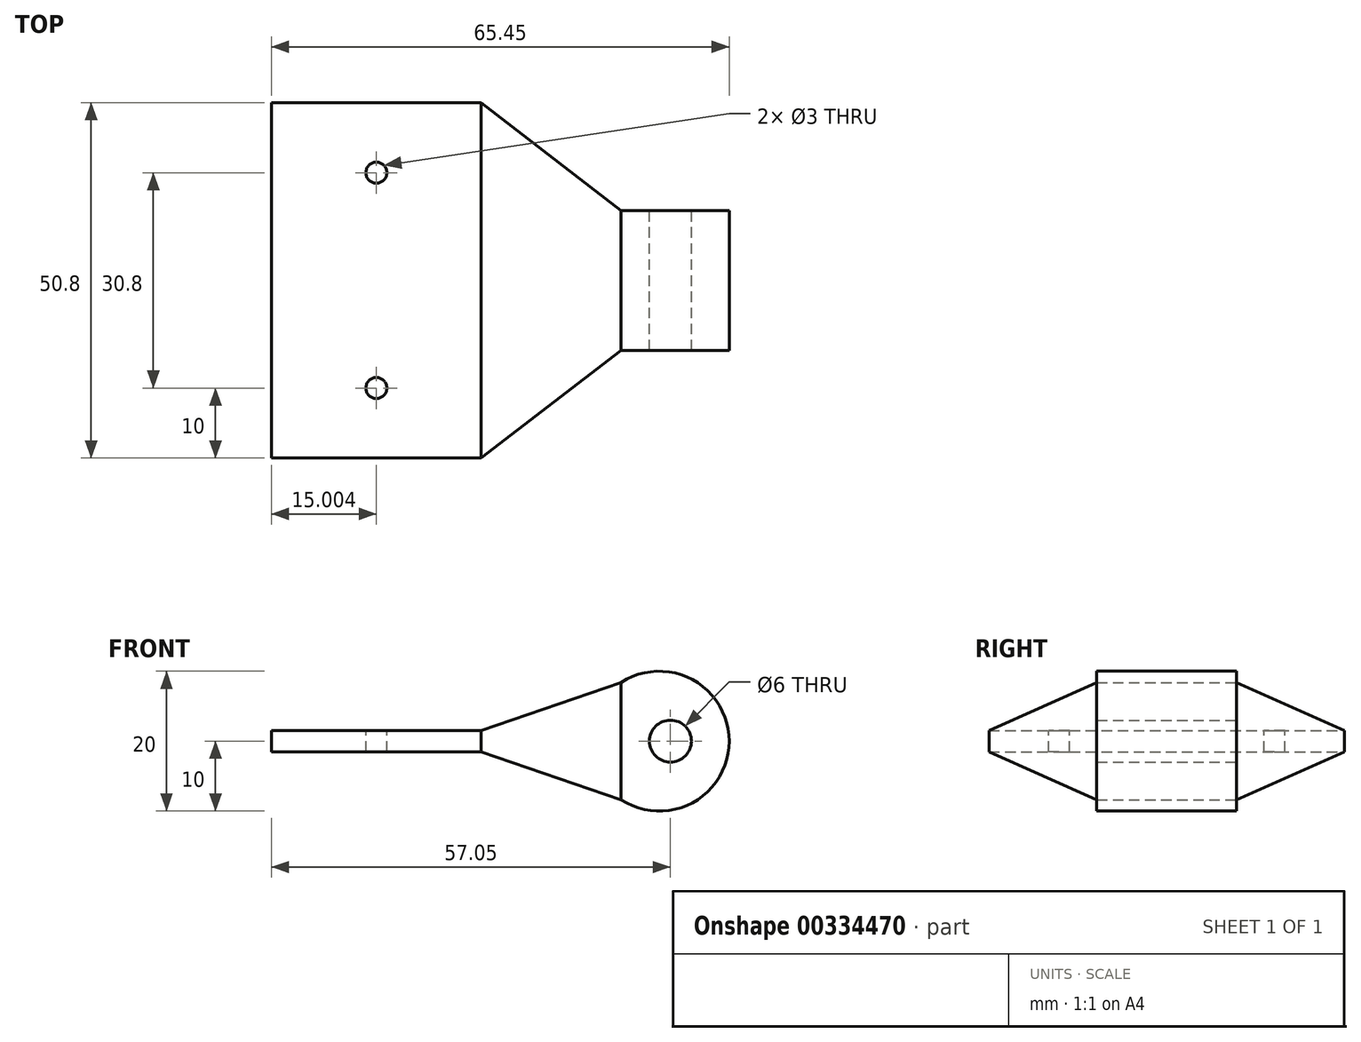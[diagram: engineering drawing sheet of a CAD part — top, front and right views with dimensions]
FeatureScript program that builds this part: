
annotation { "Feature Type Name" : "Feature", "Feature Type Description" : "" }
export const myFeature = defineFeature(function(context is Context, id is Id, definition is map)
    precondition{}
    {
        {
            var Q0;
            Q0=qCreatedBy(makeId("Front.planeOp"),FACE);
            var sketch = newSketch(context, id + "F0", { "sketchPlane" : qUnion([Q0])});
            skArc(sketch, "E0", {"start": v(-5.45, -8.39) * mm, "mid": v(10, 0) * mm, "end": v(-5.45, 8.39) * mm});
            skLineSegment(sketch, "E1", {"start": v(-5.45, 8.39) * mm, "end": v(-5.45, -8.39) * mm});
            skSolve(sketch);
        }
        {
            var Q0;
            Q0=makeQuery(id+"F0.imprint","IMPRINT",FACE,{"disambiguationData":[TD([[makeQuery(id+"F0.imprint","IMPRINT",EDGE,{"derivedFrom":sQuery(id+"F0.wireOp",EDGE,"E0")}),1.0]])]});
            extrude(context, id + "F1", {"entities" : qUnion([Q0]), "endBound" : BoundingType.SYMMETRIC, "depth" : 20 * mm, "offsetDistance" : 25 * mm});
        }
        {
            var Q0;
            Q0=makeQuery(id+"F1.opExtrude","CAP_FACE",FACE,{"disambiguationData":[OSD([sQuery(id+"F0.wireOp",EDGE,"E0"),sQuery(id+"F0.wireOp",EDGE,"E1")])],"isStart":true});
            var sketch = newSketch(context, id + "F2", { "sketchPlane" : qUnion([Q0])});
            skCircle(sketch, "E2", {"center": v(-1.6, 0) * mm, "radius": 3 * mm});
            skSolve(sketch);
        }
        {
            var Q0;
            Q0=sQuery(id+"F2.wireOp",VERTEX,"E2.center");
            var Q1;
            Q1=makeQuery(id+"F1.opExtrude","SWEPT_BODY",BODY,{"disambiguationData":[OSD([sQuery(id+"F0.wireOp",EDGE,"E0"),sQuery(id+"F0.wireOp",EDGE,"E1")])]});
            hole(context, id + "F3", {"style" : HoleStyle.SIMPLE, "endStyle" : HoleEndStyle.THROUGH, "holeDiameter" : 6 * mm, "isTappedThrough" : true, "tappedDepth" : 12 * mm, "tapClearance" : 3, "locations" : qUnion([Q0]), "scope" : qUnion([Q1])});
        }
        {
            var Q0;
            Q0=qCreatedBy(makeId("Front.planeOp"),FACE);
            var sketch = newSketch(context, id + "F4", { "sketchPlane" : qUnion([Q0])});
            skLineSegment(sketch, "E3.bottom", {"start": v(-25.45, 0) * mm, "end": v(-55.45, 0) * mm});
            skLineSegment(sketch, "E3.top", {"start": v(-25.45, 1.5) * mm, "end": v(-55.45, 1.5) * mm});
            skLineSegment(sketch, "E3.left", {"start": v(-25.45, 0) * mm, "end": v(-25.45, 1.5) * mm});
            skLineSegment(sketch, "E3.right", {"start": v(-55.45, 0) * mm, "end": v(-55.45, 1.5) * mm});
            skLineSegment(sketch, "E4.top", {"start": v(-25.45, -1.5) * mm, "end": v(-55.45, -1.5) * mm});
            skLineSegment(sketch, "E4.left", {"start": v(-25.45, 0) * mm, "end": v(-25.45, -1.5) * mm});
            skLineSegment(sketch, "E4.right", {"start": v(-55.45, 0) * mm, "end": v(-55.45, -1.5) * mm});
            skSolve(sketch);
        }
        {
            var Q0;
            Q0=makeQuery(id+"F4.imprint","IMPRINT",FACE,{"disambiguationData":[TD([[makeQuery(id+"F4.imprint","IMPRINT",EDGE,{"derivedFrom":sQuery(id+"F4.wireOp",EDGE,"E3.bottom")}),1.0]])]});
            var Q1;
            Q1=makeQuery(id+"F4.imprint","IMPRINT",FACE,{"disambiguationData":[TD([[makeQuery(id+"F4.imprint","IMPRINT",EDGE,{"derivedFrom":sQuery(id+"F4.wireOp",EDGE,"E3.top")}),1.0]])]});
            extrude(context, id + "F5", {"entities" : qUnion([Q0, Q1]), "endBound" : BoundingType.SYMMETRIC, "depth" : 50.8 * mm, "offsetDistance" : 25 * mm});
        }
        {
            var Q0;
            Q0=makeQuery(id+"F1.opExtrude","SWEPT_FACE",FACE,{"disambiguationData":[OSD([sQuery(id+"F0.wireOp",EDGE,"E1")])]});
            var Q1;
            Q1=makeQuery(id+"F5.opExtrude","SWEPT_FACE",FACE,{"disambiguationData":[OSD([sQuery(id+"F4.wireOp",EDGE,"E3.left"),sQuery(id+"F4.wireOp",EDGE,"E4.left")])]});
            loft(context, id + "F6", {"sheetProfilesArray" : [{ "sheetProfileEntities" : qUnion([Q0]) }, { "sheetProfileEntities" : qUnion([Q1]) }]});
        }
        {
            var Q0;
            Q0=makeQuery(id+"F5.opExtrude","SWEPT_FACE",FACE,{"disambiguationData":[OSD([sQuery(id+"F4.wireOp",EDGE,"E3.top")])]});
            var sketch = newSketch(context, id + "F7", { "sketchPlane" : qUnion([Q0])});
            skLineSegment(sketch, "E5", {"start": v(-40.45, 25.4) * mm, "end": v(-40.45, -25.4) * mm});
            skCircle(sketch, "E6", {"center": v(-40.45, 15.4) * mm, "radius": 1.5 * mm});
            skCircle(sketch, "E7", {"center": v(-40.45, -15.4) * mm, "radius": 1.5 * mm});
            skSolve(sketch);
        }
        {
            var Q0;
            Q0=sQuery(id+"F7.wireOp",VERTEX,"E6.center");
            var Q1;
            Q1=sQuery(id+"F7.wireOp",VERTEX,"E7.center");
            var Q2;
            Q2=makeQuery(id+"F5.opExtrude","SWEPT_BODY",BODY,{"disambiguationData":[OSD([sQuery(id+"F4.wireOp",EDGE,"E3.top"),sQuery(id+"F4.wireOp",EDGE,"E3.left"),sQuery(id+"F4.wireOp",EDGE,"E3.right"),sQuery(id+"F4.wireOp",EDGE,"E4.top"),sQuery(id+"F4.wireOp",EDGE,"E4.left"),sQuery(id+"F4.wireOp",EDGE,"E4.right")])]});
            hole(context, id + "F8", {"style" : HoleStyle.SIMPLE, "endStyle" : HoleEndStyle.THROUGH, "holeDiameter" : 3 * mm, "isTappedThrough" : true, "tappedDepth" : 12 * mm, "tapClearance" : 3, "locations" : qUnion([Q0, Q1]), "scope" : qUnion([Q2])});
        }
    });
